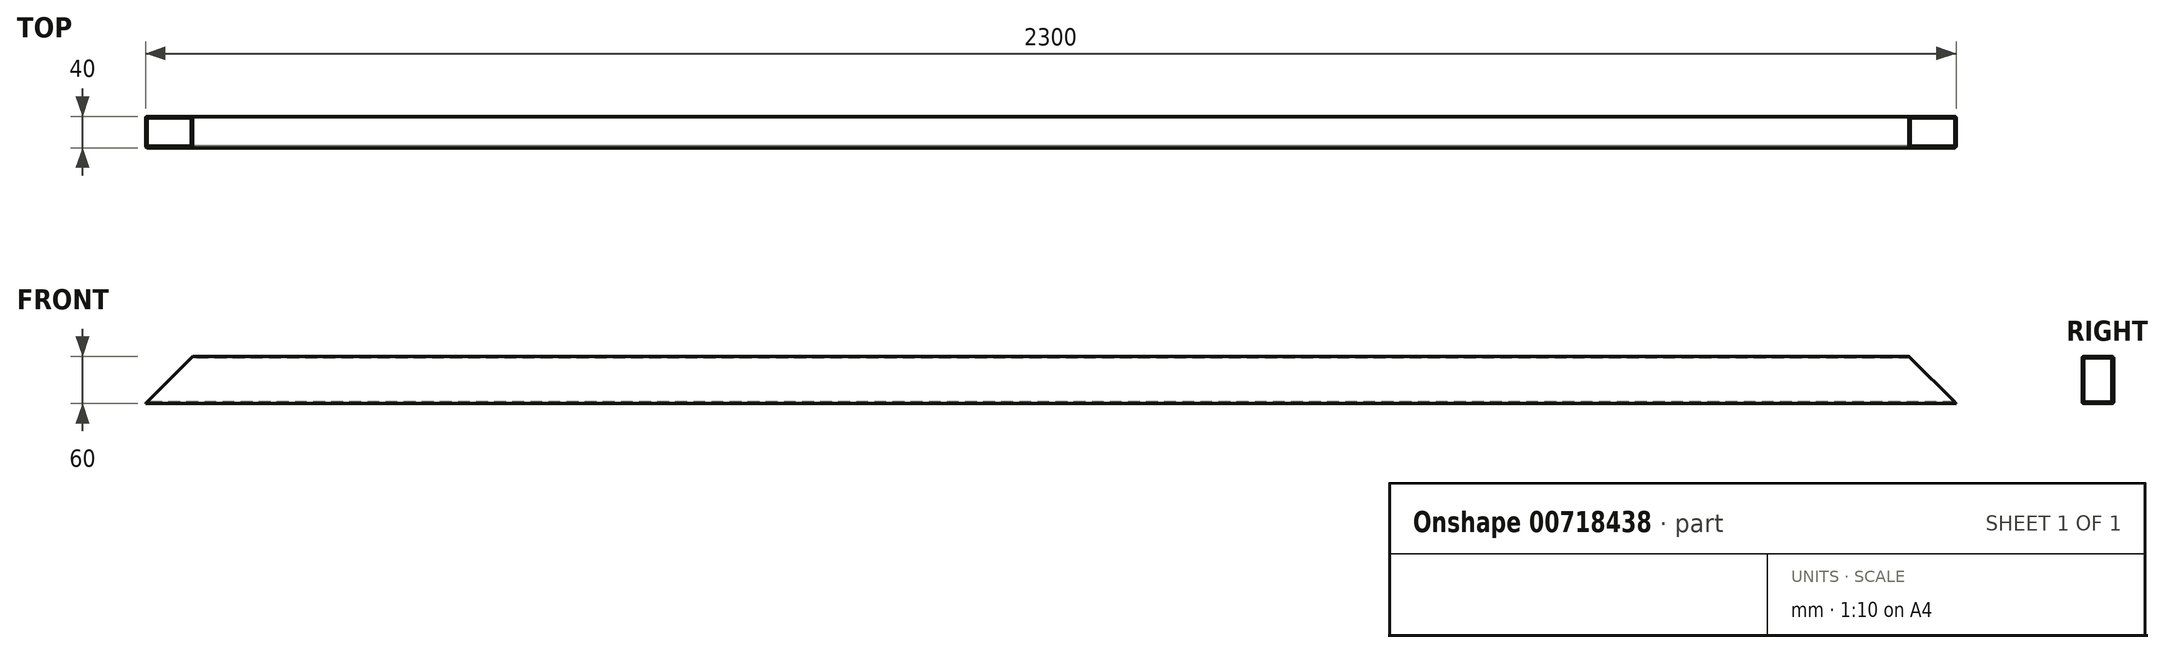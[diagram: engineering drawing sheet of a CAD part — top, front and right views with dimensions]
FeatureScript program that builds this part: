
annotation { "Feature Type Name" : "Feature", "Feature Type Description" : "" }
export const myFeature = defineFeature(function(context is Context, id is Id, definition is map)
    precondition{}
    {
        {
            var Q0;
            Q0=qCreatedBy(makeId("Right.planeOp"),FACE);
            var sketch = newSketch(context, id + "F0", { "sketchPlane" : qUnion([Q0])});
            skLineSegment(sketch, "E0.bottom", {"start": v(-18, -30) * mm, "end": v(18, -30) * mm});
            skLineSegment(sketch, "E0.top", {"start": v(-18, 30) * mm, "end": v(18, 30) * mm});
            skLineSegment(sketch, "E0.left", {"start": v(-20, -28) * mm, "end": v(-20, 28) * mm});
            skLineSegment(sketch, "E0.right", {"start": v(20, -28) * mm, "end": v(20, 28) * mm});
            skPoint(sketch, "E0.middle", {"position": v(0, 0) * mm});
            skLineSegment(sketch, "E1.bottom", {"start": v(-17, -28) * mm, "end": v(17, -28) * mm});
            skLineSegment(sketch, "E1.top", {"start": v(-17, 28) * mm, "end": v(17, 28) * mm});
            skLineSegment(sketch, "E1.left", {"start": v(-18, -27) * mm, "end": v(-18, 27) * mm});
            skLineSegment(sketch, "E1.right", {"start": v(18, -27) * mm, "end": v(18, 27) * mm});
            skPoint(sketch, "E2.visualSharp", {"position": v(-20, 30) * mm});
            skArc(sketch, "E2.filletArc", {"start": v(-18, 30) * mm, "mid": v(-19.41, 29.41) * mm, "end": v(-20, 28) * mm});
            skPoint(sketch, "E3.visualSharp", {"position": v(20, 30) * mm});
            skArc(sketch, "E3.filletArc", {"start": v(20, 28) * mm, "mid": v(19.41, 29.41) * mm, "end": v(18, 30) * mm});
            skPoint(sketch, "E4.visualSharp", {"position": v(20, -30) * mm});
            skArc(sketch, "E4.filletArc", {"start": v(18, -30) * mm, "mid": v(19.41, -29.41) * mm, "end": v(20, -28) * mm});
            skPoint(sketch, "E5.visualSharp", {"position": v(-20, -30) * mm});
            skArc(sketch, "E5.filletArc", {"start": v(-20, -28) * mm, "mid": v(-19.41, -29.41) * mm, "end": v(-18, -30) * mm});
            skArc(sketch, "E6.filletArc", {"start": v(-18, -27) * mm, "mid": v(-17.7, -27.7) * mm, "end": v(-17, -28) * mm});
            skArc(sketch, "E7.filletArc", {"start": v(-17, 28) * mm, "mid": v(-17.7, 27.7) * mm, "end": v(-18, 27) * mm});
            skArc(sketch, "E8.filletArc", {"start": v(18, 27) * mm, "mid": v(17.7, 27.7) * mm, "end": v(17, 28) * mm});
            skArc(sketch, "E9.filletArc", {"start": v(17, -28) * mm, "mid": v(17.7, -27.7) * mm, "end": v(18, -27) * mm});
            skSolve(sketch);
        }
        {
            var Q0;
            Q0=makeQuery(id+"F0.imprint","IMPRINT",FACE,{"disambiguationData":[TD([[makeQuery(id+"F0.imprint","IMPRINT",EDGE,{"derivedFrom":sQuery(id+"F0.wireOp",EDGE,"E0.bottom")}),1.0]])]});
            extrude(context, id + "F1", {"entities" : qUnion([Q0]), "depth" : 1150 * mm, "offsetDistance" : 25 * mm, "hasSecondDirection" : true, "secondDirectionOppositeDirection" : true, "secondDirectionDepth" : 1150 * mm});
        }
        {
            var Q0;
            Q0=qCreatedBy(makeId("Front.planeOp"),FACE);
            var sketch = newSketch(context, id + "F2", { "sketchPlane" : qUnion([Q0])});
            skLineSegment(sketch, "E10", {"start": v(-1150, -30) * mm, "end": v(-1150, 30) * mm});
            skLineSegment(sketch, "E11", {"start": v(-1150, 30) * mm, "end": v(-1090, 30) * mm});
            skLineSegment(sketch, "E12", {"start": v(-1090, 30) * mm, "end": v(-1150, -30) * mm});
            skLineSegment(sketch, "E13", {"start": v(0, 100.56) * mm, "end": v(0, -96.84) * mm, "construction": true});
            skLineSegment(sketch, "E14.MirrorCS", {"start": v(1150, -30) * mm, "end": v(1150, 30) * mm});
            skLineSegment(sketch, "E15.MirrorCS", {"start": v(1090, 30) * mm, "end": v(1150, -30) * mm});
            skLineSegment(sketch, "E16.MirrorCS", {"start": v(1150, 30) * mm, "end": v(1090, 30) * mm});
            skSolve(sketch);
        }
        {
            var Q0;
            Q0 = qSketchRegion(id + "F2", true);
            extrude(context, id + "F3", {"entities" : qUnion([Q0]), "operationType" : NewBodyOperationType.REMOVE, "oppositeDirection" : true, "depth" : 25 * mm, "offsetDistance" : 25 * mm, "hasSecondDirection" : true, "secondDirectionOppositeDirection" : false, "secondDirectionDepth" : 25 * mm});
        }
    });
